# Revit family: 1411001 Ottavino Wall
name_source: partatom
category: Lighting Fixtures
revit_build: Autodesk Revit 2018 (Build: 20170223_1515(x64)
units: mm (PartAtom-declared; Revit-internal decimal feet)

## family parameters
Always vertical = Yes
Cut with Voids When Loaded = No
Host = Wall
Light Source = No
OmniClass Number = 23.80.70.00
OmniClass Title = Lighting
Part Type = Normal
Room Calculation Point = No
Round Connector Dimension = Use Diameter
Shared = No

## types (2) — shared parameters
Driver Required = No
Manufacturer = Astro Lighting Ltd
Product Location = Bathroom
URL = www.astrolighting.com

## per-type parameters (varying)
| type | ADA compliant | Dimmable | Dimming Method | Electrical Class | Lamp | Location rating | Main Finish | Main Material | Power (Watts) | Product Code | Product Name | Product SKU |
| CE |  | Yes | Lamp Dependant | 1 | 5W Max E14 Candle | IP44 | Polished Chrome | Metal - Zinc | 5W Max | 0 | Ottavino Wall | 1411001 |
| ETL | NO |  |  | 0 |  | DAMP |  | Metal - Steel |  | 1234 |  | 1234001 |

## geometry (parser evidence)
native form markers: Sweep x2
no freeform markers — native parametric forms only
